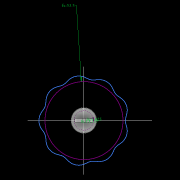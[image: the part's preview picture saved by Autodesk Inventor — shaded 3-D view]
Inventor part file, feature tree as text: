
AUTODESK INVENTOR PART (.ipt)
format: ipt  version: 2022.2 (Build 262287010, 287A)  size: 509,952 bytes
history: native  units: mm
features: other x19, extrude x16, sketch x11, pattern_circular x7, fillet x4, revolve x3, move_body x2, draft x2, plane x2, chamfer x2
ambient origin geometry x8: Origin, YZ Plane, XZ Plane, XY Plane, X Axis, Y Axis, Z Axis, Center Point
bodies: Solid5 (feature_tree), Solid6 (feature_tree)
feature tree (68):
  other  "CrossSection1"
  sketch  "Sketch7"  dims[d90=15.767323mm d167=8.972256mm d173=10.814812mm d201=53.5mm d232=0.0mm d233=3600.0mm]
  other  "Roller1"
  other  "Roller2"
  sketch  "Sketch22"  dims[d343=17.374329mm]
  sketch  "Sketch2"  dims[d56=13.336791mm d57=4.025mm]
  sketch  "Sketch23"  dims[d344=17.374602mm]
  revolve  "Revolution17"  [1 undecoded]
  extrude  "Extrusion39"  Depth=8.972256mm
  fillet  "Fillet4"  Radius=10.814812mm
  fillet  "Fillet5"  Radius=53.5mm
  other  "RevRoller1"
  fillet  "Fillet1"  Radius=3600.0mm
  pattern_circular  "Circular Pattern13"  [2 undecoded]
  move_body  "Move Body7"
  revolve  "Revolution13"  [1 undecoded]
  fillet  "Fillet3"  Radius=17.374329mm
  pattern_circular  "Circular Pattern14"  [2 undecoded]
  move_body  "Move Body6"
  revolve  "Revolution14"  [1 undecoded]
  other  "OuterRim_Top2"
  other  "OuterRim_Bottom2"
  extrude  "Rotor_Ring"  TaperAngle=90.0deg  [1 undecoded]
  draft  "FaceDraft2"
  sketch  "Sketch30"  dims[d345=0.025mm]
  plane  "Work Plane5"
  other  "Rotor Featurs"
  other  "RotorRim_Bottom"
  extrude  "Extrusion24"  Depth=0.5mm
  extrude  "Extrusion25"  Depth=0.5mm
  extrude  "Extrusion26"  TaperAngle=360.0deg  [1 undecoded]
  pattern_circular  "Circular Pattern23"  Angle=30.0deg  [1 undecoded]
  sketch  "Sketch41"  dims[d347=0.1mm]
  extrude  "Extrusion27"  Depth=0.5mm
  extrude  "Extrusion28"  Depth=0.5mm
  pattern_circular  "Circular Pattern24"  [2 undecoded]
  extrude  "Extrusion29"  Depth=0.5mm
  extrude  "Extrusion30"  TaperAngle=30.0deg  [1 undecoded]
  extrude  "Extrusion31"  TaperAngle=90.0deg  [1 undecoded]
  pattern_circular  "Circular Pattern25"  [2 undecoded]
  sketch  "Sketch42"  dims[d348=0.1mm]
  extrude  "Extrusion32"  Depth=0.5mm
  extrude  "Extrusion33"  TaperAngle=360.0deg  [1 undecoded]
  extrude  "Extrusion34"  TaperAngle=90.0deg  [1 undecoded]
  extrude  "Extrusion35"  Depth=0.5mm
  pattern_circular  "Circular Pattern26"  [2 undecoded]
  pattern_circular  "Circular Pattern27"  [2 undecoded]
  chamfer  "Chamfer1"  Distance=0.1mm
  chamfer  "Chamfer2"  Distance=0.1mm
  draft  "FaceDraft4"
  plane  "Work Plane6"
  sketch  "Sketch43"  dims[d349=17.374602mm]
  extrude  "Extrusion37"  Depth=0.5mm
  extrude  "Extrusion38"  TaperAngle=0.0deg  [1 undecoded]
  other  "2D Equation Curve1"
  sketch  "Sketch40"  dims[d346=0.025mm]
  other  "Work Axis6"
  other  "Work Axis7"
  other  "Work Axis8"
  other  "Work Axis9"
  other  "Work Axis10"
  other  "Work Point1"
  other  "Work Point2"
  other  "Work Point3"
  other  "Work Point4"
  other  "Work Point5"
  sketch  "Sketch44"  dims[d350=17.374329mm]
  sketch  "Sketch45"  dims[d351=0.025mm d352=0.025mm d354=0.1mm d355=17.374329mm d356=17.374602mm d357=1.0mm d358=90.0deg d359=0.5mm d360=60.0mm d361=360.0deg d363=30.0deg d367=8.1mm d369=4.014775mm d370=0.1mm d371=1.0mm d372=30.0deg d373=90.0deg d374=0.5mm d375=60.0mm d376=360.0deg d378=90.0deg d379=0.1mm d380=0.1mm d381=0.1mm d382=0.1mm d383=0.1mm d384=10.461905mm d385=0.0mm d386=0.0mm d391=1.0mm d392=53.5mm d393=1.5mm d394=1.5mm d395=1.5mm d396=1.5mm d397=90.0deg d398=90.0deg d399=90.0deg d400=53.5mm d401=10.461905mm d402=0.0mm d486=0.436332mm d487=0.5mm d488=2.0mm d489=0.0mm d490=20.0mm d495=2.5mm d496=8.0mm d506=13.856406mm d507=55.5mm d508=8.0mm d509=0.05mm d510=2.5mm d511=30.0deg d512=12.0mm d513=6.0mm d514=0.2mm d515=30.0deg d516=131.0mm d517=65.5mm d518=0.2mm d519=100.0mm d520=120.0mm d521=2.0mm d522=150.0mm d530=50.0mm d531=5.5mm d532=5.5mm d533=5.5mm d534=85.75mm d535=73.5mm d536=61.25mm d537=24.5mm d538=3.0mm d539=2.4mm d540=0.0mm d541=0.0mm d542=0.0mm d543=5.5mm d544=3.0mm d545=0.0mm d546=90.0mm d547=360.0deg d549=3.0mm d550=3.0mm d551=2.4mm d552=0.0mm d553=5.230953mm d554=0.0mm d555=2.4mm d556=0.0mm d557=5.230953mm d558=0.0mm d559=5.230953mm d560=0.0mm d561=90.0mm d562=360.0deg d564=60.0mm d565=360.0deg d567=5.5mm d568=5.5mm d569=3.0mm d570=0.0mm d571=5.230953mm d572=0.0mm d573=3.0mm d574=0.0mm d575=5.230953mm d576=0.0mm d577=90.0mm d578=360.0deg d580=60.0mm d581=360.0deg d584=20.0mm d585=8.0mm d587=1.75mm d589=3.0mm d592=2.0mm d593=12.0mm d594=12.0mm d600=0.5mm d601=2.0mm d602=45.0deg d603=0.5mm d604=2.0mm d605=45.0deg d606=0.436332mm d607=0.5mm d608=0.0mm d609=20.0mm d611=360.0deg d613=0.0mm d614=0.0mm d615=0.1mm d616=90.0deg d617=25.0mm d618=5.0mm d619=25.0mm d620=0.0mm d621=10.0mm d622=0.5mm d16=0.872665mm d17=0.872665mm d49=0.872665mm d50=0.872665mm d51=0.872665mm d52=0.872665mm d236=0.5mm d237=0.872665mm d238=0.5mm d239=0.872665mm d282=1.0mm d283=1.0mm d284=1.0mm d285=0.15mm d286=0.25mm d287=0.375mm d288=14.3117mm d289=0.75mm d290=20.594885mm d291=0.0625mm d292=0.75mm d293=0.375mm d405=0.5mm d406=0.872665mm d407=0.5mm d408=0.872665mm d413=0.5mm d414=0.872665mm d415=0.5mm d416=0.872665mm d417=0.5mm d418=0.872665mm d419=0.5mm d420=0.872665mm d421=0.872665mm d431=0.5mm d432=0.872665mm d433=0.5mm d434=0.872665mm d471=0.5mm d472=0.872665mm d473=0.5mm d474=0.872665mm d497=0.5mm d498=0.872665mm d499=0.5mm d500=0.872665mm d590=0.5mm d591=0.872665mm]
note: 23 required parameter values undecoded (feature->parameter linkage not recoverable at this tier; creation-order binding heuristic only, values carry confidence <= 0.55)